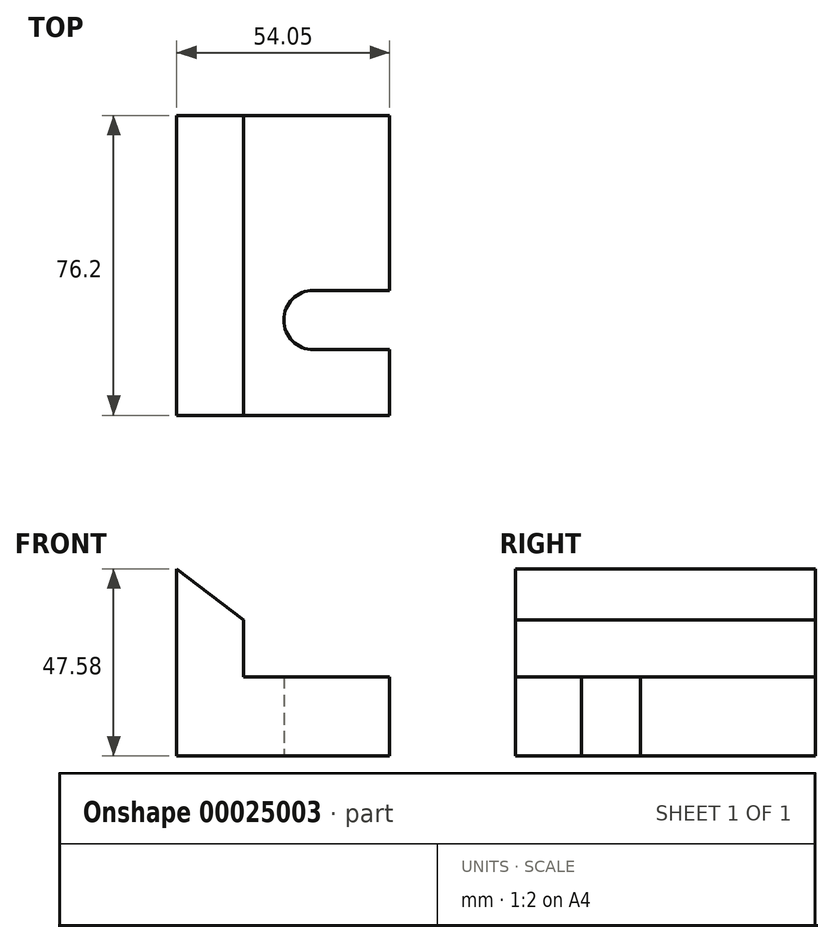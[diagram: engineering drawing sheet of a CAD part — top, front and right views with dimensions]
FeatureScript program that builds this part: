
annotation { "Feature Type Name" : "Feature", "Feature Type Description" : "" }
export const myFeature = defineFeature(function(context is Context, id is Id, definition is map)
    precondition{}
    {
        {
            var Q0;
            Q0=qCreatedBy(makeId("Front.planeOp"),FACE);
            var sketch = newSketch(context, id + "F0", { "sketchPlane" : qUnion([Q0])});
            skLineSegment(sketch, "E0", {"start": v(0, 0) * mm, "end": v(0, 47.58) * mm});
            skLineSegment(sketch, "E1", {"start": v(0, 47.58) * mm, "end": v(16.99, 34.65) * mm});
            skLineSegment(sketch, "E2", {"start": v(16.99, 34.65) * mm, "end": v(16.99, 20.17) * mm});
            skLineSegment(sketch, "E3", {"start": v(16.99, 20.17) * mm, "end": v(54.05, 20.17) * mm});
            skLineSegment(sketch, "E4", {"start": v(54.05, 20.17) * mm, "end": v(54.05, 0) * mm});
            skLineSegment(sketch, "E5", {"start": v(54.05, 0) * mm, "end": v(0, 0) * mm});
            skSolve(sketch);
        }
        {
            var Q0;
            Q0=makeQuery(id+"F0.imprint","IMPRINT",FACE,{"disambiguationData":[TD([[makeQuery(id+"F0.imprint","IMPRINT",EDGE,{"derivedFrom":sQuery(id+"F0.wireOp",EDGE,"E0")}),-1.0]])]});
            extrude(context, id + "F1", {"entities" : qUnion([Q0]), "oppositeDirection" : true, "depth" : 76.2 * mm});
        }
        {
            var Q0;
            Q0=qCreatedBy(makeId("Top.planeOp"),FACE);
            var sketch = newSketch(context, id + "F2", { "sketchPlane" : qUnion([Q0])});
            skLineSegment(sketch, "E6.0.0", {"start": v(16.99, 0) * mm, "end": v(54.05, 0) * mm});
            skLineSegment(sketch, "E6.0.1", {"start": v(54.05, 0) * mm, "end": v(54.05, 76.2) * mm});
            skLineSegment(sketch, "E6.0.2", {"start": v(54.05, 76.2) * mm, "end": v(16.99, 76.2) * mm});
            skLineSegment(sketch, "E6.0.3", {"start": v(16.99, 76.2) * mm, "end": v(16.99, 0) * mm});
            skLineSegment(sketch, "E7.bottom", {"start": v(54.05, 16.7) * mm, "end": v(34.74, 16.7) * mm});
            skLineSegment(sketch, "E7.top", {"start": v(54.05, 31.75) * mm, "end": v(34.74, 31.75) * mm});
            skLineSegment(sketch, "E7.left", {"start": v(54.05, 16.7) * mm, "end": v(54.05, 31.75) * mm});
            skLineSegment(sketch, "E7.right", {"start": v(34.74, 16.7) * mm, "end": v(34.74, 31.75) * mm});
            skCircle(sketch, "E8", {"center": v(34.74, 24.22) * mm, "radius": 7.53 * mm});
            skSolve(sketch);
        }
        {
            var Q0;
            {var subQ1=sQuery(id+"F2.wireOp",EDGE,"E7.right");Q0=makeQuery(id+"F2.imprint","IMPRINT",FACE,{"disambiguationData":[TD([[makeQuery(id+"F2.imprint","IMPRINT",EDGE,{"derivedFrom":subQ1}),-1.0]])]});}
            var Q1;
            {var subQ1=sQuery(id+"F2.wireOp",EDGE,"E7.right");Q1=makeQuery(id+"F2.imprint","IMPRINT",FACE,{"disambiguationData":[TD([[makeQuery(id+"F2.imprint","IMPRINT",EDGE,{"derivedFrom":subQ1}),1.0]])]});}
            var Q2;
            {var subQ3=sQuery(id+"F2.wireOp",EDGE,"E7.bottom");Q2=makeQuery(id+"F2.imprint","IMPRINT",FACE,{"disambiguationData":[TD([[makeQuery(id+"F2.imprint","IMPRINT",EDGE,{"derivedFrom":subQ3}),-1.0]])]});}
            extrude(context, id + "F3", {"entities" : qUnion([Q0, Q1, Q2]), "operationType" : NewBodyOperationType.REMOVE, "endBound" : BoundingType.THROUGH_ALL, "depth" : 25.4 * mm});
        }
    });
